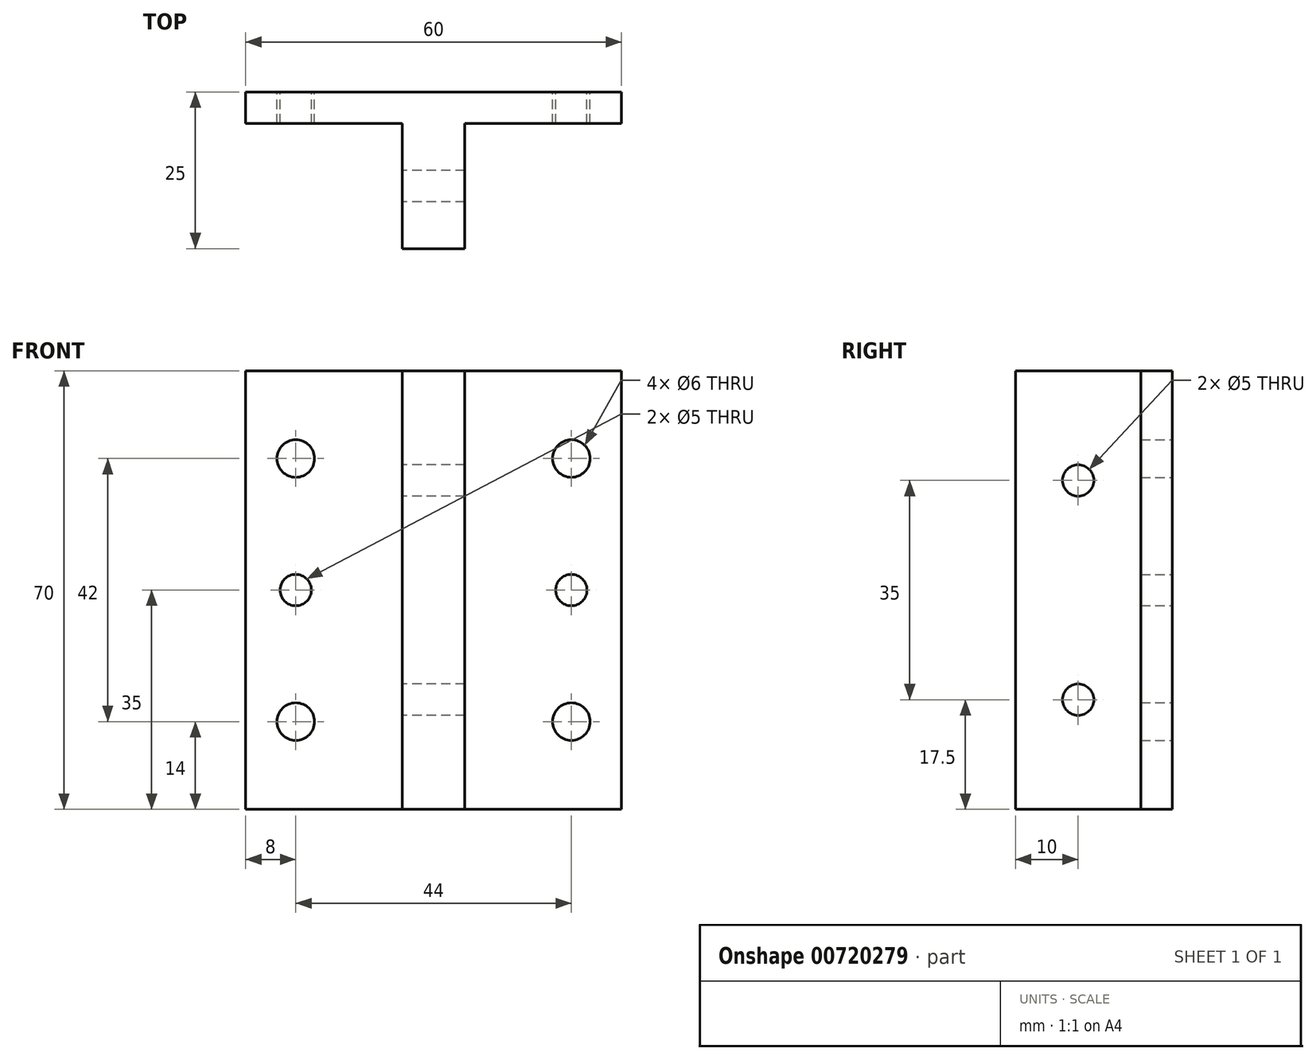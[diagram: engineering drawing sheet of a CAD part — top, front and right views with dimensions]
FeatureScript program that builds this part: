
annotation { "Feature Type Name" : "Feature", "Feature Type Description" : "" }
export const myFeature = defineFeature(function(context is Context, id is Id, definition is map)
    precondition{}
    {
        {
            var Q0;
            Q0=qCreatedBy(makeId("Front.planeOp"),FACE);
            var sketch = newSketch(context, id + "F0", { "sketchPlane" : qUnion([Q0])});
            skLineSegment(sketch, "E0.bottom", {"start": v(30, 35) * mm, "end": v(-30, 35) * mm});
            skLineSegment(sketch, "E0.top", {"start": v(30, -35) * mm, "end": v(-30, -35) * mm});
            skLineSegment(sketch, "E0.left", {"start": v(30, 35) * mm, "end": v(30, -35) * mm});
            skLineSegment(sketch, "E0.right", {"start": v(-30, 35) * mm, "end": v(-30, -35) * mm});
            skPoint(sketch, "E0.middle", {"position": v(0, 0) * mm});
            skCircle(sketch, "E1", {"center": v(-22, 21) * mm, "radius": 3 * mm});
            skCircle(sketch, "E2", {"center": v(-22, 0) * mm, "radius": 2.5 * mm});
            skCircle(sketch, "E3", {"center": v(-22, -21) * mm, "radius": 3 * mm});
            skCircle(sketch, "E4", {"center": v(22, 21) * mm, "radius": 3 * mm});
            skCircle(sketch, "E5", {"center": v(22, 0) * mm, "radius": 2.5 * mm});
            skCircle(sketch, "E6", {"center": v(22, -21) * mm, "radius": 3 * mm});
            skSolve(sketch);
        }
        {
            var Q0;
            Q0=makeQuery(id+"F0.imprint","IMPRINT",FACE,{"disambiguationData":[TD([[makeQuery(id+"F0.imprint","IMPRINT",EDGE,{"derivedFrom":sQuery(id+"F0.wireOp",EDGE,"E0.bottom")}),1.0]])]});
            extrude(context, id + "F1", {"entities" : qUnion([Q0]), "depth" : 5 * mm, "offsetDistance" : 25 * mm});
        }
        {
            var Q0;
            Q0=makeQuery(id+"F1.opExtrude","CAP_FACE",FACE,{"disambiguationData":[OSD([sQuery(id+"F0.wireOp",EDGE,"E0.bottom"),sQuery(id+"F0.wireOp",EDGE,"E0.top"),sQuery(id+"F0.wireOp",EDGE,"E0.left"),sQuery(id+"F0.wireOp",EDGE,"E0.right"),sQuery(id+"F0.wireOp",EDGE,"E1"),sQuery(id+"F0.wireOp",EDGE,"E2"),sQuery(id+"F0.wireOp",EDGE,"E3"),sQuery(id+"F0.wireOp",EDGE,"E4"),sQuery(id+"F0.wireOp",EDGE,"E5"),sQuery(id+"F0.wireOp",EDGE,"E6")])],"isStart":false});
            var sketch = newSketch(context, id + "F2", { "sketchPlane" : qUnion([Q0])});
            skLineSegment(sketch, "E7.bottom", {"start": v(-10, 35) * mm, "end": v(-5, 35) * mm});
            skLineSegment(sketch, "E7.top", {"start": v(-10, -165) * mm, "end": v(-5, -165) * mm});
            skLineSegment(sketch, "E7.left", {"start": v(-10, 35) * mm, "end": v(-10, -165) * mm});
            skLineSegment(sketch, "E7.right", {"start": v(-5, 35) * mm, "end": v(-5, -165) * mm});
            skLineSegment(sketch, "E8.bottom", {"start": v(5, 35) * mm, "end": v(10, 35) * mm});
            skLineSegment(sketch, "E8.top", {"start": v(5, -165) * mm, "end": v(10, -165) * mm});
            skLineSegment(sketch, "E8.left", {"start": v(5, 35) * mm, "end": v(5, -165) * mm});
            skLineSegment(sketch, "E8.right", {"start": v(10, 35) * mm, "end": v(10, -165) * mm});
            skSolve(sketch);
        }
        {
            var Q0;
            {var subQ0=sQuery(id+"F2.wireOp",EDGE,"E7.right");var subQ3=makeQuery(id+"F1.opExtrude","CAP_EDGE",EDGE,{"disambiguationData":[OSD([sQuery(id+"F0.wireOp",EDGE,"E0.top")])],"isStart":false});var subQ4=makeQuery(id+"F2.imprint","INTERSECT",VERTEX,{"derivedFrom":[subQ3,subQ0]});Q0=makeQuery(id+"F2.imprint","IMPRINT",FACE,{"disambiguationData":[TD([[makeQuery(id+"F2.imprint","IMPRINT",EDGE,{"disambiguationData":[TD([[subQ4,1.0]])],"derivedFrom":subQ3}),-1.0]])]});}
            extrude(context, id + "F3", {"entities" : qUnion([Q0]), "operationType" : NewBodyOperationType.ADD, "depth" : 20 * mm, "offsetDistance" : 25 * mm});
        }
        {
            var Q0;
            Q0=makeQuery(id+"F3.opExtrude","SWEPT_FACE",FACE,{"disambiguationData":[OSD([sQuery(id+"F2.wireOp",EDGE,"E8.left")])]});
            var sketch = newSketch(context, id + "F4", { "sketchPlane" : qUnion([Q0])});
            skPoint(sketch, "E9", {"position": v(-15, 17.5) * mm});
            skPoint(sketch, "E10", {"position": v(-15, -17.5) * mm});
            skSolve(sketch);
        }
        {
            var Q0;
            Q0=sQuery(id+"F4.wireOp",VERTEX,"E9");
            var Q1;
            Q1=sQuery(id+"F4.wireOp",VERTEX,"E10");
            var Q2;
            Q2=makeQuery(id+"F1.opExtrude","SWEPT_BODY",BODY,{"disambiguationData":[OSD([sQuery(id+"F0.wireOp",EDGE,"E0.bottom"),sQuery(id+"F0.wireOp",EDGE,"E0.top"),sQuery(id+"F0.wireOp",EDGE,"E0.left"),sQuery(id+"F0.wireOp",EDGE,"E0.right"),sQuery(id+"F0.wireOp",EDGE,"E1"),sQuery(id+"F0.wireOp",EDGE,"E2"),sQuery(id+"F0.wireOp",EDGE,"E3"),sQuery(id+"F0.wireOp",EDGE,"E4"),sQuery(id+"F0.wireOp",EDGE,"E5"),sQuery(id+"F0.wireOp",EDGE,"E6")])]});
            hole(context, id + "F5", {"style" : HoleStyle.SIMPLE, "endStyle" : HoleEndStyle.BLIND, "holeDiameter" : 5 * mm, "majorDiameter" : 5 * mm, "holeDepth" : 40 * mm, "tappedDepth" : 12 * mm, "tapClearance" : 3, "locations" : qUnion([Q0, Q1]), "scope" : qUnion([Q2])});
        }
    });
